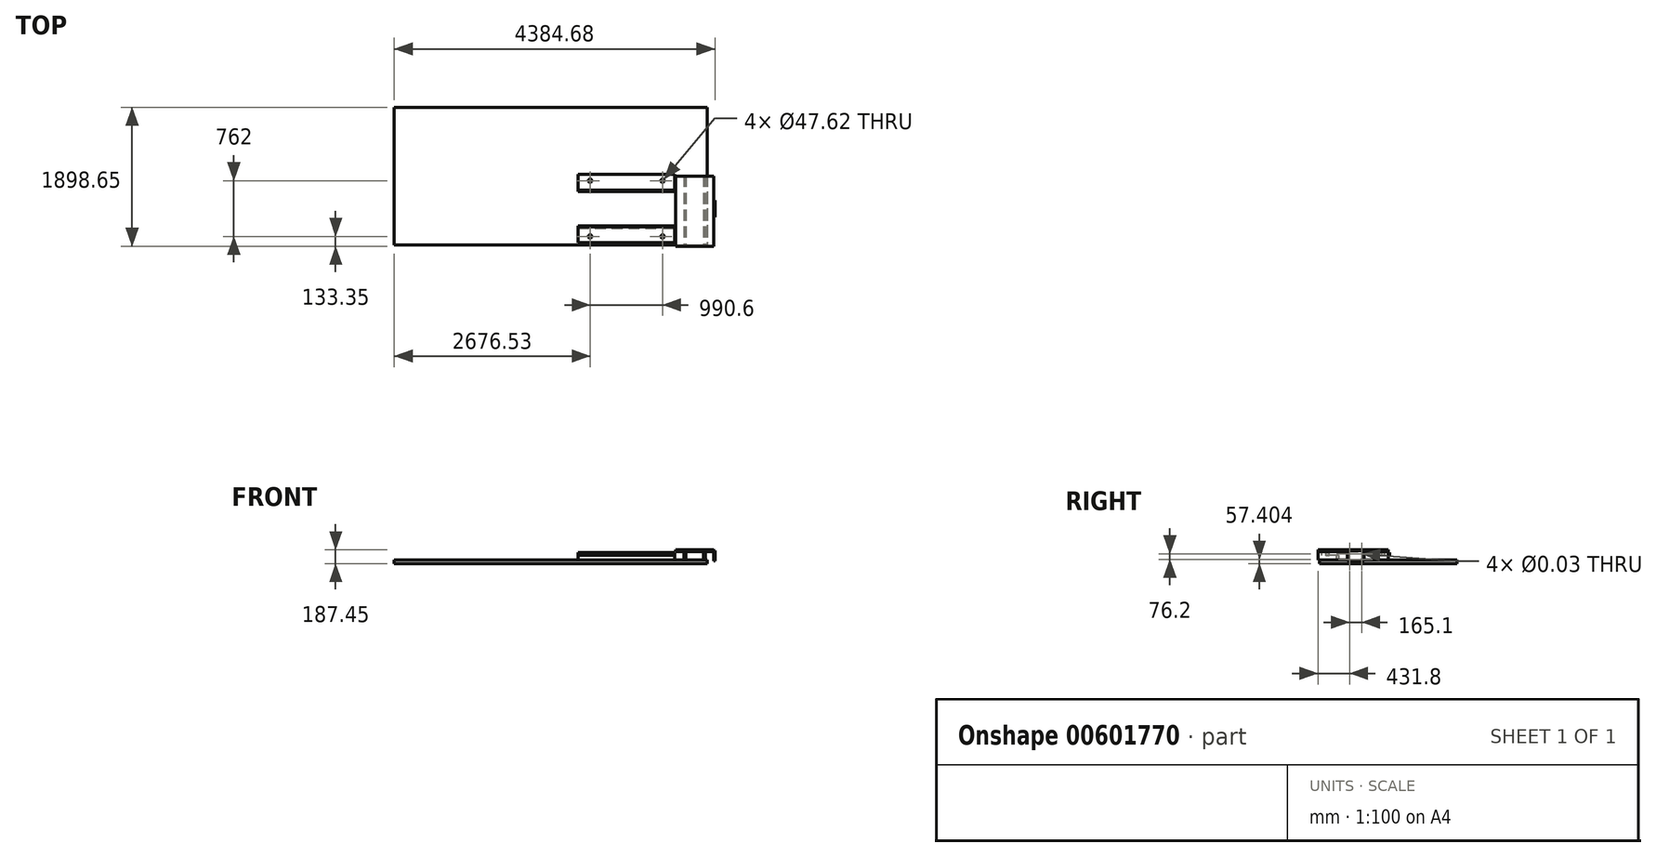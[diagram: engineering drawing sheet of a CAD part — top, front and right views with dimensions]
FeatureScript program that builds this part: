
annotation { "Feature Type Name" : "Feature", "Feature Type Description" : "" }
export const myFeature = defineFeature(function(context is Context, id is Id, definition is map)
    precondition{}
    {
        {
            var Q0;
            Q0=qCreatedBy(makeId("Top.planeOp"),FACE);
            var sketch = newSketch(context, id + "F0", { "sketchPlane" : qUnion([Q0])});
            skLineSegment(sketch, "E0.bottom", {"start": v(-2139.95, 939.8) * mm, "end": v(2139.95, 939.8) * mm});
            skLineSegment(sketch, "E0.top", {"start": v(-2139.95, -939.8) * mm, "end": v(2139.95, -939.8) * mm});
            skLineSegment(sketch, "E0.left", {"start": v(-2139.95, 939.8) * mm, "end": v(-2139.95, -939.8) * mm});
            skLineSegment(sketch, "E0.right", {"start": v(2139.95, 939.8) * mm, "end": v(2139.95, -939.8) * mm});
            skPoint(sketch, "E0.middle", {"position": v(0, 0) * mm});
            skSolve(sketch);
        }
        {
            var Q0;
            Q0=qSketchRegion(id+"F0",true);
            extrude(context, id + "F1", {"entities" : qUnion([Q0]), "oppositeDirection" : true, "depth" : 50.8 * mm, "offsetDistance" : 25.4 * mm});
        }
        {
            var Q0;
            Q0=makeQuery(id+"F1.opExtrude","CAP_FACE",FACE,{"disambiguationData":[OSD([sQuery(id+"F0.wireOp",EDGE,"E0.bottom"),sQuery(id+"F0.wireOp",EDGE,"E0.top"),sQuery(id+"F0.wireOp",EDGE,"E0.left"),sQuery(id+"F0.wireOp",EDGE,"E0.right")])],"isStart":true});
            var sketch = newSketch(context, id + "F2", { "sketchPlane" : qUnion([Q0])});
            skLineSegment(sketch, "E1.0", {"start": v(1031.87, 939.8) * mm, "end": v(1031.87, -939.8) * mm, "construction": true});
            skLineSegment(sketch, "E2", {"start": v(-2139.95, 0) * mm, "end": v(2139.95, 0) * mm, "construction": true});
            skLineSegment(sketch, "E3.0", {"start": v(-2139.95, -444.5) * mm, "end": v(2139.95, -444.5) * mm, "construction": true});
            skLineSegment(sketch, "E4.0", {"start": v(-2139.95, -679.45) * mm, "end": v(2139.95, -679.45) * mm, "construction": true});
            skLineSegment(sketch, "E5.0", {"start": v(371.47, 939.8) * mm, "end": v(371.47, -939.8) * mm, "construction": true});
            skLineSegment(sketch, "E6.bottom", {"start": v(371.47, -679.45) * mm, "end": v(1692.27, -679.45) * mm});
            skLineSegment(sketch, "E6.top", {"start": v(371.47, -711.2) * mm, "end": v(1692.27, -711.2) * mm});
            skLineSegment(sketch, "E6.left", {"start": v(371.47, -679.45) * mm, "end": v(371.47, -711.2) * mm});
            skLineSegment(sketch, "E6.right", {"start": v(1692.27, -679.45) * mm, "end": v(1692.27, -711.2) * mm});
            skLineSegment(sketch, "E7.MirrorCS", {"start": v(371.47, -209.55) * mm, "end": v(371.47, -177.8) * mm});
            skLineSegment(sketch, "E8.MirrorCS", {"start": v(1692.27, -209.55) * mm, "end": v(1692.27, -177.8) * mm});
            skLineSegment(sketch, "E9.MirrorCS", {"start": v(371.47, -177.8) * mm, "end": v(1692.27, -177.8) * mm});
            skLineSegment(sketch, "E10.MirrorCS", {"start": v(371.47, -209.55) * mm, "end": v(1692.27, -209.55) * mm});
            skSolve(sketch);
        }
        {
            var Q0;
            Q0=qSketchRegion(id+"F2",true);
            extrude(context, id + "F3", {"entities" : qUnion([Q0]), "operationType" : NewBodyOperationType.ADD, "depth" : 63.5 * mm, "offsetDistance" : 25.4 * mm});
        }
        {
            var Q0;
            Q0=makeQuery(id+"F3.opExtrude","CAP_FACE",FACE,{"disambiguationData":[OSD([sQuery(id+"F2.wireOp",EDGE,"E6.bottom"),sQuery(id+"F2.wireOp",EDGE,"E6.top"),sQuery(id+"F2.wireOp",EDGE,"E6.left"),sQuery(id+"F2.wireOp",EDGE,"E6.right")])],"isStart":false});
            var sketch = newSketch(context, id + "F4", { "sketchPlane" : qUnion([Q0])});
            skLineSegment(sketch, "E11.0", {"start": v(-2139.95, -444.5) * mm, "end": v(2139.95, -444.5) * mm, "construction": true});
            skLineSegment(sketch, "E12.0", {"start": v(-2139.95, -695.45) * mm, "end": v(2139.95, -695.45) * mm, "construction": true});
            skLineSegment(sketch, "E13.0", {"start": v(371.47, 939.8) * mm, "end": v(371.47, -939.8) * mm, "construction": true});
            skLineSegment(sketch, "E14.bottom", {"start": v(371.47, -695.45) * mm, "end": v(1692.27, -695.45) * mm});
            skLineSegment(sketch, "E14.top", {"start": v(371.47, -911.35) * mm, "end": v(1692.27, -911.35) * mm});
            skLineSegment(sketch, "E14.left", {"start": v(371.47, -695.45) * mm, "end": v(371.47, -911.35) * mm});
            skLineSegment(sketch, "E14.right", {"start": v(1692.27, -695.45) * mm, "end": v(1692.27, -911.35) * mm});
            skLineSegment(sketch, "E15.MirrorCS", {"start": v(1692.27, -193.55) * mm, "end": v(1692.27, 22.35) * mm});
            skLineSegment(sketch, "E16.MirrorCS", {"start": v(371.47, -193.55) * mm, "end": v(371.47, 22.35) * mm});
            skLineSegment(sketch, "E17.MirrorCS", {"start": v(371.47, 22.35) * mm, "end": v(1692.27, 22.35) * mm});
            skLineSegment(sketch, "E18.MirrorCS", {"start": v(371.47, -193.55) * mm, "end": v(1692.27, -193.55) * mm});
            skSolve(sketch);
        }
        {
            var Q0;
            Q0=qSketchRegion(id+"F4",true);
            extrude(context, id + "F5", {"entities" : qUnion([Q0]), "operationType" : NewBodyOperationType.ADD, "depth" : 38.1 * mm, "offsetDistance" : 25.4 * mm});
        }
        {
            var Q0;
            Q0=makeQuery(id+"F5.opExtrude","CAP_FACE",FACE,{"disambiguationData":[OSD([sQuery(id+"F4.wireOp",EDGE,"E14.bottom"),sQuery(id+"F4.wireOp",EDGE,"E14.top"),sQuery(id+"F4.wireOp",EDGE,"E14.left"),sQuery(id+"F4.wireOp",EDGE,"E14.right")])],"isStart":false});
            var sketch = newSketch(context, id + "F6", { "sketchPlane" : qUnion([Q0])});
            skLineSegment(sketch, "E19.0", {"start": v(-2139.95, -444.5) * mm, "end": v(2139.95, -444.5) * mm, "construction": true});
            skLineSegment(sketch, "E20.0", {"start": v(1031.87, 939.8) * mm, "end": v(1031.87, -939.8) * mm, "construction": true});
            skLineSegment(sketch, "E21.0", {"start": v(-2139.95, -825.5) * mm, "end": v(2139.95, -825.5) * mm, "construction": true});
            skLineSegment(sketch, "E22.0", {"start": v(536.57, 939.8) * mm, "end": v(536.57, -939.8) * mm, "construction": true});
            skPoint(sketch, "E23", {"position": v(536.57, -825.5) * mm});
            skPoint(sketch, "E24.0.1.0", {"position": v(536.57, -63.5) * mm});
            skPoint(sketch, "E24.1.0.0", {"position": v(1527.17, -825.5) * mm});
            skPoint(sketch, "E24.1.1.0", {"position": v(1527.17, -63.5) * mm});
            skLineSegment(sketch, "E24.direction1", {"start": v(536.57, -825.5) * mm, "end": v(1527.17, -825.5) * mm, "construction": true});
            skLineSegment(sketch, "E24.direction2", {"start": v(536.57, -825.5) * mm, "end": v(536.57, -63.5) * mm, "construction": true});
            skSolve(sketch);
        }
        {
            var Q0;
            Q0=sQuery(id+"F6.wireOp",VERTEX,"E24.0.1.0");
            var Q1;
            Q1=sQuery(id+"F6.wireOp",VERTEX,"E24.1.1.0");
            var Q2;
            Q2=sQuery(id+"F6.wireOp",VERTEX,"E23");
            var Q3;
            Q3=sQuery(id+"F6.wireOp",VERTEX,"E24.1.0.0");
            var Q4;
            Q4=makeQuery(id+"F1.opExtrude","SWEPT_BODY",BODY,{"disambiguationData":[OSD([sQuery(id+"F0.wireOp",EDGE,"E0.bottom"),sQuery(id+"F0.wireOp",EDGE,"E0.top"),sQuery(id+"F0.wireOp",EDGE,"E0.left"),sQuery(id+"F0.wireOp",EDGE,"E0.right")])]});
            hole(context, id + "F7", {"style" : HoleStyle.SIMPLE, "endStyle" : HoleEndStyle.BLIND, "holeDiameter" : 47.62 * mm, "majorDiameter" : 6.35 * mm, "holeDepth" : 50.8 * mm, "isTappedThrough" : true, "tappedDepth" : 25.4 * mm, "tapClearance" : 3, "locations" : qUnion([Q0, Q1, Q2, Q3]), "scope" : qUnion([Q4])});
        }
        {
            var Q0;
            Q0=makeQuery(id+"F1.opExtrude","CAP_FACE",FACE,{"disambiguationData":[OSD([sQuery(id+"F0.wireOp",EDGE,"E0.bottom"),sQuery(id+"F0.wireOp",EDGE,"E0.top"),sQuery(id+"F0.wireOp",EDGE,"E0.left"),sQuery(id+"F0.wireOp",EDGE,"E0.right")])],"isStart":true});
            var sketch = newSketch(context, id + "F8", { "sketchPlane" : qUnion([Q0])});
            skLineSegment(sketch, "E25.0", {"start": v(-2139.95, -444.5) * mm, "end": v(2139.95, -444.5) * mm, "construction": true});
            skLineSegment(sketch, "E26.0", {"start": v(1031.87, 939.8) * mm, "end": v(1031.87, -939.8) * mm, "construction": true});
            skLineSegment(sketch, "E27.0", {"start": v(1965.33, 939.8) * mm, "end": v(1965.32, -939.8) * mm, "construction": true});
            skLineSegment(sketch, "E28.0", {"start": v(1844.67, 0) * mm, "end": v(1844.67, -958.85) * mm});
            skLineSegment(sketch, "E29.0", {"start": v(1819.27, 0) * mm, "end": v(1819.27, -958.85) * mm});
            skLineSegment(sketch, "E30.0", {"start": v(1819.27, -958.85) * mm, "end": v(1844.67, -958.85) * mm});
            skLineSegment(sketch, "E31.0", {"start": v(-2139.95, 0) * mm, "end": v(1031.87, 0) * mm});
            skLineSegment(sketch, "E32.trimOffspring", {"start": v(1819.27, 0) * mm, "end": v(1844.67, 0) * mm});
            skLineSegment(sketch, "E33.MirrorCS", {"start": v(2111.37, -958.85) * mm, "end": v(2085.97, -958.85) * mm});
            skLineSegment(sketch, "E34.MirrorCS", {"start": v(2111.37, 0) * mm, "end": v(2085.97, 0) * mm});
            skLineSegment(sketch, "E35.MirrorCS", {"start": v(2085.97, 0) * mm, "end": v(2085.97, -958.85) * mm});
            skLineSegment(sketch, "E36.MirrorCS", {"start": v(2111.37, 0) * mm, "end": v(2111.37, -958.85) * mm});
            skSolve(sketch);
        }
        {
            var Q0;
            Q0=qSketchRegion(id+"F8",true);
            extrude(context, id + "F9", {"entities" : qUnion([Q0]), "operationType" : NewBodyOperationType.ADD, "depth" : 111.25 * mm, "offsetDistance" : 25.4 * mm});
        }
        {
            var Q0;
            Q0=makeQuery(id+"F9.opExtrude","CAP_FACE",FACE,{"disambiguationData":[OSD([sQuery(id+"F8.wireOp",EDGE,"E28.0"),sQuery(id+"F8.wireOp",EDGE,"E29.0"),sQuery(id+"F8.wireOp",EDGE,"E30.0"),sQuery(id+"F8.wireOp",EDGE,"E32.trimOffspring")])],"isStart":false});
            var sketch = newSketch(context, id + "F10", { "sketchPlane" : qUnion([Q0])});
            skLineSegment(sketch, "E37.0", {"start": v(1965.33, 939.8) * mm, "end": v(1965.32, -939.8) * mm, "construction": true});
            skLineSegment(sketch, "E38.0", {"start": v(-2139.95, -444.5) * mm, "end": v(2139.95, -444.5) * mm, "construction": true});
            skLineSegment(sketch, "E39.bottom", {"start": v(1704.97, -958.85) * mm, "end": v(2225.67, -958.85) * mm});
            skLineSegment(sketch, "E39.top", {"start": v(1704.97, 0) * mm, "end": v(2225.67, 0) * mm});
            skLineSegment(sketch, "E39.left", {"start": v(1704.97, -958.85) * mm, "end": v(1704.97, 0) * mm});
            skLineSegment(sketch, "E39.right", {"start": v(2225.67, -958.85) * mm, "end": v(2225.67, 0) * mm});
            skPoint(sketch, "E39.middle", {"position": v(1965.32, -479.42) * mm});
            skLineSegment(sketch, "E40.0", {"start": v(1031.87, 939.8) * mm, "end": v(1031.87, -939.8) * mm, "construction": true});
            skSolve(sketch);
        }
        {
            var Q0;
            Q0=qSketchRegion(id+"F10",true);
            extrude(context, id + "F11", {"entities" : qUnion([Q0]), "operationType" : NewBodyOperationType.ADD, "depth" : 25.4 * mm, "offsetDistance" : 25.4 * mm});
        }
        {
            var Q0;
            Q0=makeQuery(id+"F11.opExtrude","SWEPT_FACE",FACE,{"disambiguationData":[OSD([sQuery(id+"F10.wireOp",EDGE,"E39.right")])]});
            var sketch = newSketch(context, id + "F12", { "sketchPlane" : qUnion([Q0])});
            skPoint(sketch, "E41.0", {"position": v(-193.55, 82.55) * mm});
            skPoint(sketch, "E42.0", {"position": v(-695.45, 82.55) * mm});
            skLineSegment(sketch, "E43", {"start": v(-695.45, 82.55) * mm, "end": v(-193.55, 82.55) * mm, "construction": true});
            skLineSegment(sketch, "E44", {"start": v(-444.5, 82.55) * mm, "end": v(-444.5, 269.72) * mm, "construction": true});
            skLineSegment(sketch, "E45.0", {"start": v(-558.8, 127) * mm, "end": v(-330.2, 127) * mm});
            skLineSegment(sketch, "E46.0", {"start": v(-558.8, -12.7) * mm, "end": v(-330.2, -12.7) * mm});
            skLineSegment(sketch, "E47.0", {"start": v(-330.2, -12.7) * mm, "end": v(-330.2, 127) * mm});
            skLineSegment(sketch, "E48.MirrorCS", {"start": v(-558.8, -12.7) * mm, "end": v(-558.8, 127) * mm});
            skSolve(sketch);
        }
        {
            var Q0;
            Q0=qSketchRegion(id+"F12",true);
            extrude(context, id + "F13", {"entities" : qUnion([Q0]), "operationType" : NewBodyOperationType.ADD, "depth" : 19.05 * mm, "offsetDistance" : 25.4 * mm});
        }
        {
            var Q0;
            Q0=makeQuery(id+"F13.opExtrude","CAP_FACE",FACE,{"disambiguationData":[OSD([sQuery(id+"F12.wireOp",EDGE,"E45.0"),sQuery(id+"F12.wireOp",EDGE,"E46.0"),sQuery(id+"F12.wireOp",EDGE,"E47.0"),sQuery(id+"F12.wireOp",EDGE,"E48.MirrorCS")])],"isStart":false});
            var sketch = newSketch(context, id + "F14", { "sketchPlane" : qUnion([Q0])});
            skLineSegment(sketch, "E49.0", {"start": v(-958.85, 82.8) * mm, "end": v(0, 82.8) * mm, "construction": true});
            skLineSegment(sketch, "E50.0", {"start": v(-958.85, 6.6) * mm, "end": v(0, 6.6) * mm, "construction": true});
            skLineSegment(sketch, "E51", {"start": v(-444.5, -12.7) * mm, "end": v(-444.5, 245.05) * mm, "construction": true});
            skLineSegment(sketch, "E52.0", {"start": v(-361.95, -12.7) * mm, "end": v(-361.95, 245.05) * mm, "construction": true});
            skLineSegment(sketch, "E53.MirrorCS", {"start": v(-527.05, -12.7) * mm, "end": v(-527.05, 245.05) * mm, "construction": true});
            skPoint(sketch, "E54", {"position": v(-527.05, 6.6) * mm});
            skPoint(sketch, "E55", {"position": v(-527.05, 82.8) * mm});
            skPoint(sketch, "E56", {"position": v(-361.95, 82.8) * mm});
            skPoint(sketch, "E57", {"position": v(-361.95, 6.6) * mm});
            skSolve(sketch);
        }
        {
            var Q0;
            Q0=sQuery(id+"F14.wireOp",VERTEX,"E55");
            var Q1;
            Q1=sQuery(id+"F14.wireOp",VERTEX,"E54");
            var Q2;
            Q2=sQuery(id+"F14.wireOp",VERTEX,"E57");
            var Q3;
            Q3=sQuery(id+"F14.wireOp",VERTEX,"E56");
            var Q4;
            Q4=makeQuery(id+"F1.opExtrude","SWEPT_BODY",BODY,{"disambiguationData":[OSD([sQuery(id+"F0.wireOp",EDGE,"E0.bottom"),sQuery(id+"F0.wireOp",EDGE,"E0.top"),sQuery(id+"F0.wireOp",EDGE,"E0.left"),sQuery(id+"F0.wireOp",EDGE,"E0.right")])]});
            hole(context, id + "F15", {"style" : HoleStyle.SIMPLE, "endStyle" : HoleEndStyle.BLIND, "standardTappedOrClearance" : lookupTablePath({ "standard" : "ANSI", "size" : "11/16 (0.69)", "type" : "Drilled" }), "standardBlindInLast" : lookupTablePath({ "standard" : "ANSI", "size" : "11/16", "type" : "Drilled" }), "holeDiameter" : 11 / 406.4 * mm, "majorDiameter" : 6.35 * mm, "holeDepth" : 50.8 * mm, "isTappedThrough" : true, "tappedDepth" : 25.4 * mm, "tapClearance" : 3, "locations" : qUnion([Q0, Q1, Q2, Q3]), "scope" : qUnion([Q4])});
        }
    });
